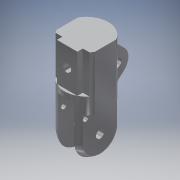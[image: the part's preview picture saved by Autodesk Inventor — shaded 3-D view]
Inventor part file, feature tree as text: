
AUTODESK INVENTOR PART (.ipt)
format: ipt  version: 2019 (Build 230136000, 136)  size: 188,416 bytes
history: imported  units: in
note: dims shown in document units (in); Inventor stores cm internally (conversion verified against a paired STEP export)
features: imported_body x1
ambient origin geometry x8: Origin, YZ Plane, XZ Plane, XY Plane, X Axis, Y Axis, Z Axis, Center Point
bodies: Solid1 (imported_parasolid), Body (imported_parasolid)
feature tree (1):
  imported_body  NMx_Import_Brep_tag  [imported B-rep: ~5 faces, bbox_mm=None]
